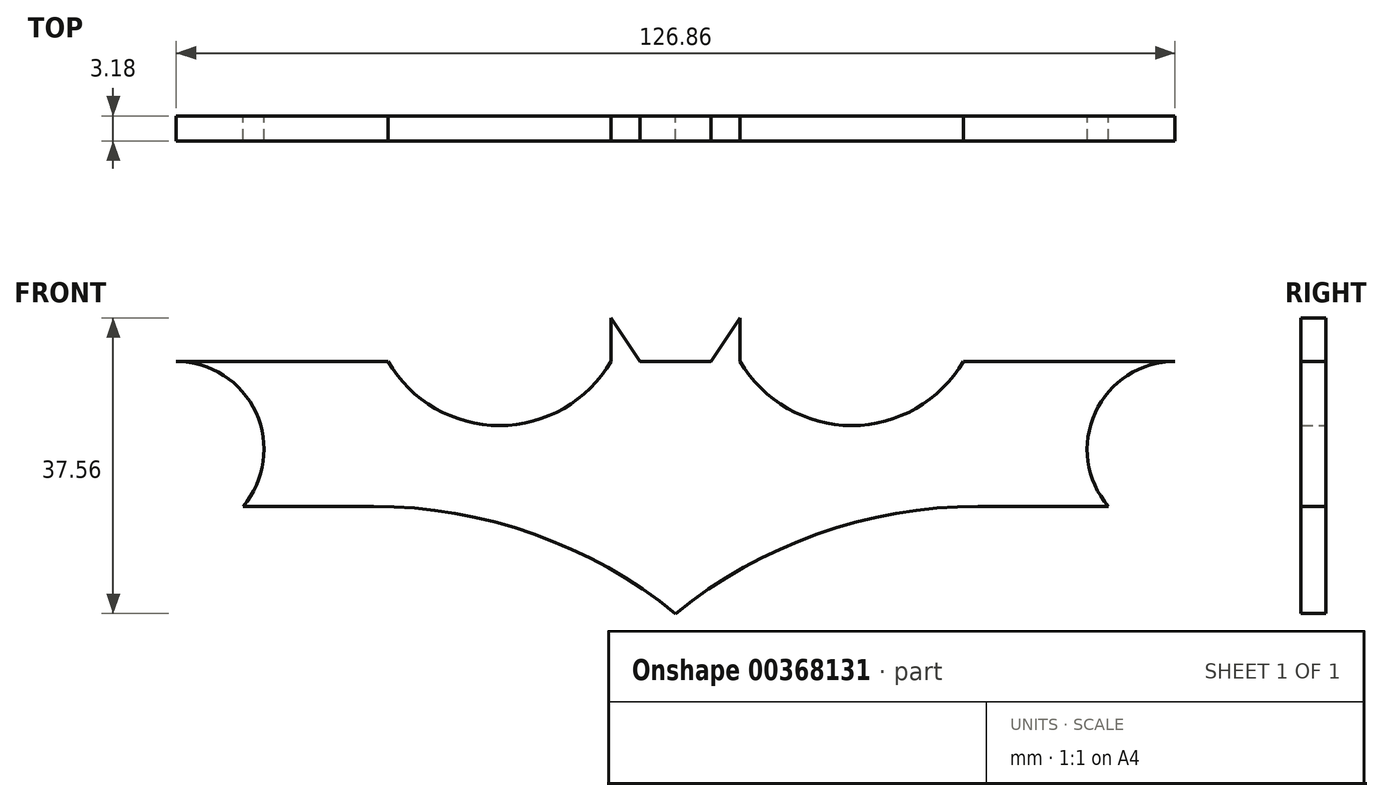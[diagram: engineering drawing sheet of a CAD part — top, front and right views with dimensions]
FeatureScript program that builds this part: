
annotation { "Feature Type Name" : "Feature", "Feature Type Description" : "" }
export const myFeature = defineFeature(function(context is Context, id is Id, definition is map)
    precondition{}
    {
        {
            var Q0;
            Q0=qCreatedBy(makeId("Front.planeOp"),FACE);
            var sketch = newSketch(context, id + "F0", { "sketchPlane" : qUnion([Q0])});
            skLineSegment(sketch, "E0", {"start": v(0, 39.66) * mm, "end": v(4.52, 39.66) * mm});
            skLineSegment(sketch, "E1", {"start": v(4.52, 39.66) * mm, "end": v(8.2, 45.19) * mm});
            skLineSegment(sketch, "E2", {"start": v(8.2, 45.19) * mm, "end": v(8.2, 39.66) * mm});
            skArc(sketch, "E3", {"start": v(8.2, 39.66) * mm, "mid": v(22.38, 31.53) * mm, "end": v(36.55, 39.66) * mm});
            skLineSegment(sketch, "E4", {"start": v(36.55, 39.66) * mm, "end": v(63.43, 39.66) * mm});
            skArc(sketch, "E5", {"start": v(63.43, 39.66) * mm, "mid": v(53.3, 33.17) * mm, "end": v(54.96, 21.25) * mm});
            skLineSegment(sketch, "E6", {"start": v(54.96, 21.25) * mm, "end": v(38.4, 21.25) * mm});
            skArc(sketch, "E7", {"start": v(38.4, 21.25) * mm, "mid": v(18.02, 17.75) * mm, "end": v(0, 7.63) * mm});
            skLineSegment(sketch, "E8", {"start": v(0, 39.66) * mm, "end": v(0, 7.63) * mm, "construction": true});
            skLineSegment(sketch, "E9.MirrorCS", {"start": v(0, 39.66) * mm, "end": v(-4.52, 39.66) * mm});
            skLineSegment(sketch, "E10.MirrorCS", {"start": v(-4.52, 39.66) * mm, "end": v(-8.2, 45.19) * mm});
            skLineSegment(sketch, "E11.MirrorCS", {"start": v(-8.2, 45.19) * mm, "end": v(-8.2, 39.66) * mm});
            skArc(sketch, "E12.MirrorCS", {"start": v(-8.2, 39.66) * mm, "mid": v(-22.38, 31.53) * mm, "end": v(-36.55, 39.66) * mm});
            skLineSegment(sketch, "E13.MirrorCS", {"start": v(-36.55, 39.66) * mm, "end": v(-63.43, 39.66) * mm});
            skArc(sketch, "E14.MirrorCS", {"start": v(-63.43, 39.66) * mm, "mid": v(-53.3, 33.17) * mm, "end": v(-54.96, 21.25) * mm});
            skLineSegment(sketch, "E15.MirrorCS", {"start": v(-54.96, 21.25) * mm, "end": v(-38.4, 21.25) * mm});
            skArc(sketch, "E16.MirrorCS", {"start": v(-38.4, 21.25) * mm, "mid": v(-18.02, 17.75) * mm, "end": v(0, 7.63) * mm});
            skSolve(sketch);
        }
        {
            var Q0;
            Q0 = qSketchRegion(id + "F0", true);
            extrude(context, id + "F1", {"entities" : qUnion([Q0]), "endBound" : BoundingType.SYMMETRIC, "depth" : 3.17 * mm});
        }
    });
